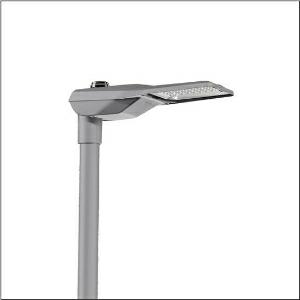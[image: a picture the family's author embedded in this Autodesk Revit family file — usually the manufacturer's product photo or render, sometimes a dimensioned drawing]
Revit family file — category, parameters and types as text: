
# Revit family: streetlight_sl_21_mini___st1_5a_5xe6p37n08gb_e583
name_source: partatom
category: Lighting Fixtures
units: mm (PartAtom-declared; Revit-internal decimal feet)

## family parameters
Cut with Voids When Loaded = No
Host = Face
Light Source = No
Part Type = Normal
Room Calculation Point = No
Round Connector Dimension = Use Diameter
Shared = No

## types (1)
- --- (1 x LED, 5840 lm, 40.4 W, 3000K)
    Apparent Load = 40 VA
    CIE Flux Codes = 22 53 95 100 100
    Color Rendering = 70
    Color Temperature = 3000K
    Default Elevation = 1800 mm
    Description = Streetlight SL 21 mini, mast luminaire, primary light control with lens, of PMMA, primary optical cover: cover, of toughened safety glass, transparent, light distribution: ST1.5a, light emission: direct distribution, primary light characteristic: asymmetric, installation type: side-entry, LED, 3G 1.5mm², High Power LED, rated luminous flux: 5.840lm, luminous efficacy: 145lm/W, light colour: 730, colour temperature: 3000K, control gear: NEMA (7pin), control: overheat protection, pre-setting: linear dimming characteristic, constant luminous flux control, time-dependent luminous flux control, flexible luminous flux parameterisation, mains connection: 230..240V, AC, 50/60Hz, connection cable pre-assembled, cable length: 8,5m, wiring characteristics: H07RN-F, start of lifetime: 40W, end of service life: 41W, reduction: 19W, luminaire housing, of diecast aluminium (EN AC-44300), powder-coated, Siteco® metallic grey (DB 702S), corrosivity category C5 mid according to DIN EN ISO 12944, multi-level sealing system, sealing non-destructively replaceable, inclination adjustable: 0°, 5°, 10°, 15°, length: 628mm, width: 235mm, height: 110mm, spigot size: 42mm (side-entry), mounting height: 4..8m, protection rating (complete): IP66, insulation class (complete): insulation class I (protective earthing), certification: CE, ENEC, ENEC+, VDE, impact resistance: IK10, permissible operating ambient temperature for outdoor applications: -40..+50°C, standard-compliant lighting for roads and squares, packaging unit: 1 piece

Light Distribution: ST1.5a
    Height = 110 mm
    Lamp = 1 x LED
    Lamp Light Flux = 5840 lm
    Lamp Power = 40.4 W
    Lamp count = 1
    Length = 625 mm
    Luminous efficacy = 145 lm/W
    Manufacturer = Siteco
    ModVariant = No
    Model = 5XE6P37N08GB
    Number of Poles = 1
    OnlyDefault = Yes
    Power Factor = 1
    Product Name = Streetlight SL 21 mini | ST1.5a
    Product group = mast luminaire | pylon top
    ProductGroupID = 6100
    Protection Class = Protection class I
    Protection Degree = IP 66
    RLX_Detail_Level = 1
    RLX_Emergency_Light_Flux = 0 lm
    RLX_Emergency_Type = 0
    RLX_Emergency_Type_DB = No
    RlxData = <blob elided: 29421 chars, md5=5c01e2c9>
    Socket = socket
    Standby Power = 0 W
    System Light Flux = 5840 lm
    System Power = 40 W
    Type Comments = factory setting: luminous flux: 100 % | dim-lin: 254 | 812 mA
    Type Image = l_1294379.jpg
    URL = http://relux.com
    VarID = @adj_133658
    Voltage = 0 V
    Weight = 0.00 kg
    Width = 234 mm

## geometry (parser evidence)
native form markers: Blend x4, Sweep x10
no freeform markers — native parametric forms only
